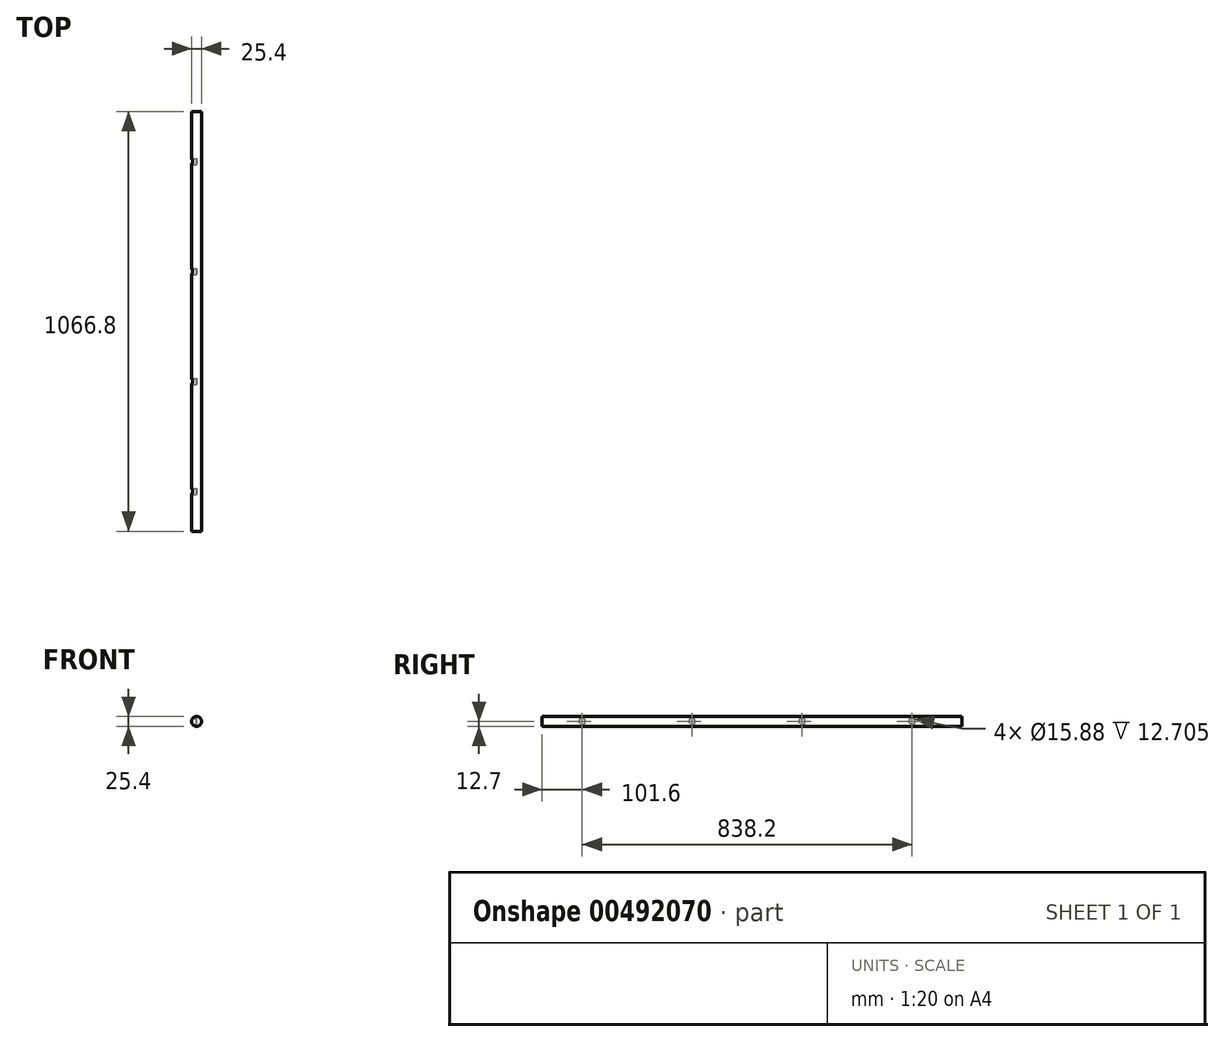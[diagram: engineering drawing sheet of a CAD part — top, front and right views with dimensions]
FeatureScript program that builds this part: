
annotation { "Feature Type Name" : "Feature", "Feature Type Description" : "" }
export const myFeature = defineFeature(function(context is Context, id is Id, definition is map)
    precondition{}
    {
        {
            var Q0;
            Q0=qCreatedBy(makeId("Front.planeOp"),FACE);
            var sketch = newSketch(context, id + "F0", { "sketchPlane" : qUnion([Q0])});
            skCircle(sketch, "E0", {"center": v(0, 0) * mm, "radius": 12.7 * mm});
            skCircle(sketch, "E1", {"center": v(0, 0) * mm, "radius": 11.18 * mm, "construction": true});
            skSolve(sketch);
        }
        {
            var Q0;
            Q0=makeQuery(id+"F0.imprint","IMPRINT",FACE,{"disambiguationData":[TD([[makeQuery(id+"F0.imprint","IMPRINT",EDGE,{"derivedFrom":sQuery(id+"F0.wireOp",EDGE,"E0")}),1.0]])]});
            extrude(context, id + "F1", {"entities" : qUnion([Q0]), "depth" : 1066.8 * mm});
        }
        {
            var Q0;
            Q0=qCreatedBy(makeId("Right.planeOp"),FACE);
            var sketch = newSketch(context, id + "F2", { "sketchPlane" : qUnion([Q0])});
            skLineSegment(sketch, "E2", {"start": v(-1066.8, 0) * mm, "end": v(0, 0) * mm, "construction": true});
            skCircle(sketch, "E3", {"center": v(-406.4, 0) * mm, "radius": 7.94 * mm});
            skCircle(sketch, "E4", {"center": v(-685.8, 0) * mm, "radius": 7.94 * mm});
            skCircle(sketch, "E5", {"center": v(-965.2, 0) * mm, "radius": 7.94 * mm});
            skCircle(sketch, "E6", {"center": v(-127, 0) * mm, "radius": 7.94 * mm});
            skSolve(sketch);
        }
        {
            var Q0;
            Q0 = qSketchRegion(id + "F2", true);
            extrude(context, id + "F3", {"entities" : qUnion([Q0]), "operationType" : NewBodyOperationType.REMOVE, "oppositeDirection" : true, "depth" : 25.4 * mm});
        }
    });
